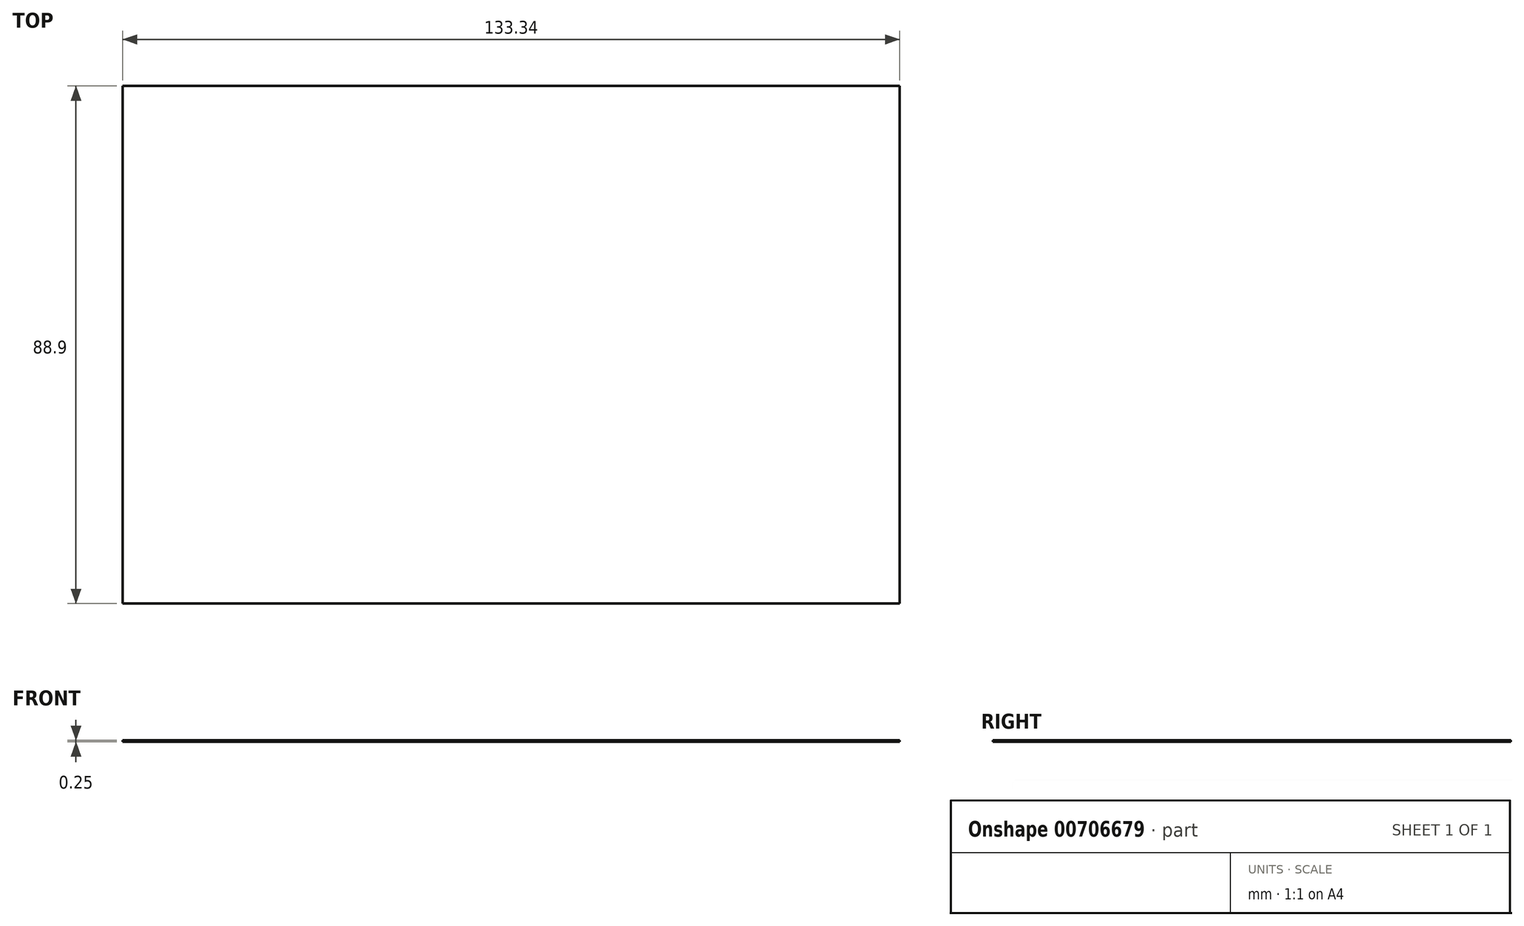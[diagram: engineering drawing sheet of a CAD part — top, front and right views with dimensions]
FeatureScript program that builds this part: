
annotation { "Feature Type Name" : "Feature", "Feature Type Description" : "" }
export const myFeature = defineFeature(function(context is Context, id is Id, definition is map)
    precondition{}
    {
        {
            var Q0;
            Q0=qCreatedBy(makeId("Top.planeOp"),FACE);
            var sketch = newSketch(context, id + "F0", { "sketchPlane" : qUnion([Q0])});
            skLineSegment(sketch, "E0.bottom", {"start": v(-66.67, 44.45) * mm, "end": v(66.68, 44.45) * mm});
            skLineSegment(sketch, "E0.top", {"start": v(-66.68, -44.45) * mm, "end": v(66.68, -44.45) * mm});
            skLineSegment(sketch, "E0.left", {"start": v(-66.67, 44.45) * mm, "end": v(-66.68, -44.45) * mm});
            skLineSegment(sketch, "E0.right", {"start": v(66.68, 44.45) * mm, "end": v(66.68, -44.45) * mm});
            skPoint(sketch, "E0.middle", {"position": v(0, 0) * mm});
            skSolve(sketch);
        }
        {
            var Q0;
            Q0=makeQuery(id+"F0.imprint","IMPRINT",FACE,{"disambiguationData":[TD([[makeQuery(id+"F0.imprint","IMPRINT",EDGE,{"derivedFrom":sQuery(id+"F0.wireOp",EDGE,"E0.bottom")}),-1.0]])]});
            extrude(context, id + "F1", {"entities" : qUnion([Q0]), "depth" : 0.25 * mm, "offsetDistance" : 25.4 * mm});
        }
    });
